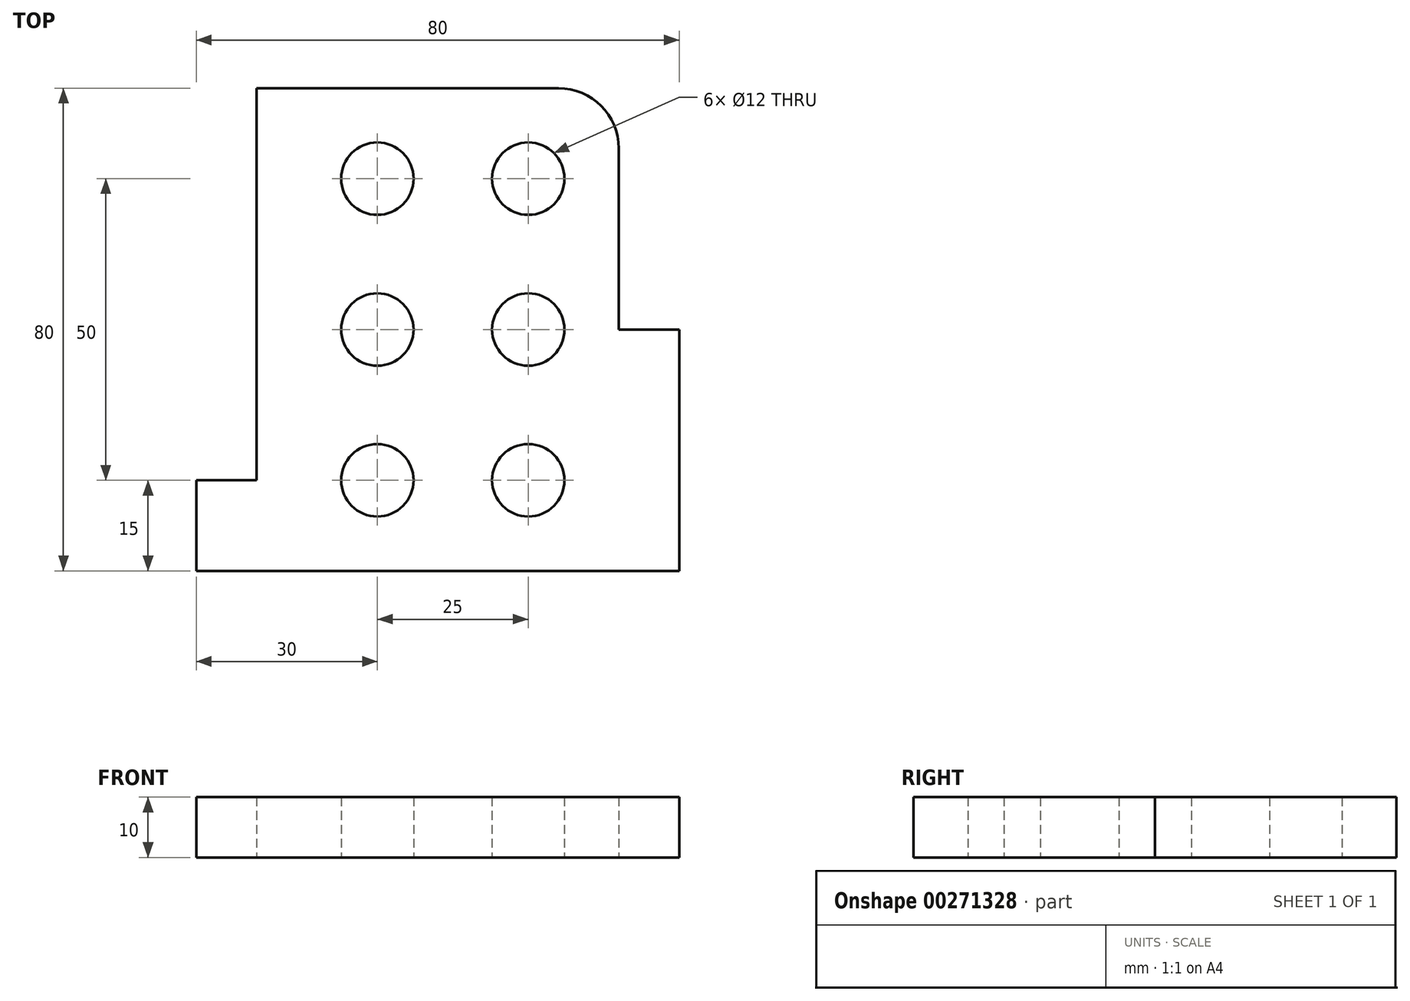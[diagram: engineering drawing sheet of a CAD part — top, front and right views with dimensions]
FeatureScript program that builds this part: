
annotation { "Feature Type Name" : "Feature", "Feature Type Description" : "" }
export const myFeature = defineFeature(function(context is Context, id is Id, definition is map)
    precondition{}
    {
        {
            var Q0;
            Q0=qCreatedBy(makeId("Top.planeOp"),FACE);
            var sketch = newSketch(context, id + "F0", { "sketchPlane" : qUnion([Q0])});
            skLineSegment(sketch, "E0", {"start": v(0, 0) * mm, "end": v(80, 0) * mm});
            skLineSegment(sketch, "E1", {"start": v(80, 0) * mm, "end": v(80, 40) * mm});
            skLineSegment(sketch, "E2", {"start": v(0, 0) * mm, "end": v(0, 15) * mm});
            skLineSegment(sketch, "E3", {"start": v(0, 15) * mm, "end": v(10, 15) * mm});
            skLineSegment(sketch, "E4", {"start": v(10, 15) * mm, "end": v(10, 80) * mm});
            skLineSegment(sketch, "E5", {"start": v(10, 80) * mm, "end": v(60, 80) * mm});
            skArc(sketch, "E6", {"start": v(60, 80) * mm, "mid": v(67.07, 77.07) * mm, "end": v(70, 70) * mm});
            skLineSegment(sketch, "E7", {"start": v(70, 70) * mm, "end": v(70, 40) * mm});
            skLineSegment(sketch, "E8", {"start": v(70, 40) * mm, "end": v(80, 40) * mm});
            skCircle(sketch, "E9", {"center": v(30, 65) * mm, "radius": 6 * mm});
            skCircle(sketch, "E10", {"center": v(55, 65) * mm, "radius": 6 * mm});
            skCircle(sketch, "E11", {"center": v(30, 40) * mm, "radius": 6 * mm});
            skCircle(sketch, "E12", {"center": v(55, 40) * mm, "radius": 6 * mm});
            skCircle(sketch, "E13", {"center": v(30, 15) * mm, "radius": 6 * mm});
            skCircle(sketch, "E14", {"center": v(55, 15) * mm, "radius": 6 * mm});
            skLineSegment(sketch, "E15", {"start": v(30, 65) * mm, "end": v(30, 15) * mm, "construction": true});
            skLineSegment(sketch, "E16", {"start": v(30, 15) * mm, "end": v(55, 15) * mm, "construction": true});
            skLineSegment(sketch, "E17", {"start": v(55, 15) * mm, "end": v(55, 65) * mm, "construction": true});
            skLineSegment(sketch, "E18", {"start": v(55, 65) * mm, "end": v(30, 65) * mm, "construction": true});
            skLineSegment(sketch, "E19", {"start": v(30, 40) * mm, "end": v(55, 40) * mm, "construction": true});
            skSolve(sketch);
        }
        {
            var Q0;
            Q0 = qSketchRegion(id + "F0", true);
            extrude(context, id + "F1", {"entities" : qUnion([Q0]), "depth" : 10 * mm});
        }
    });
